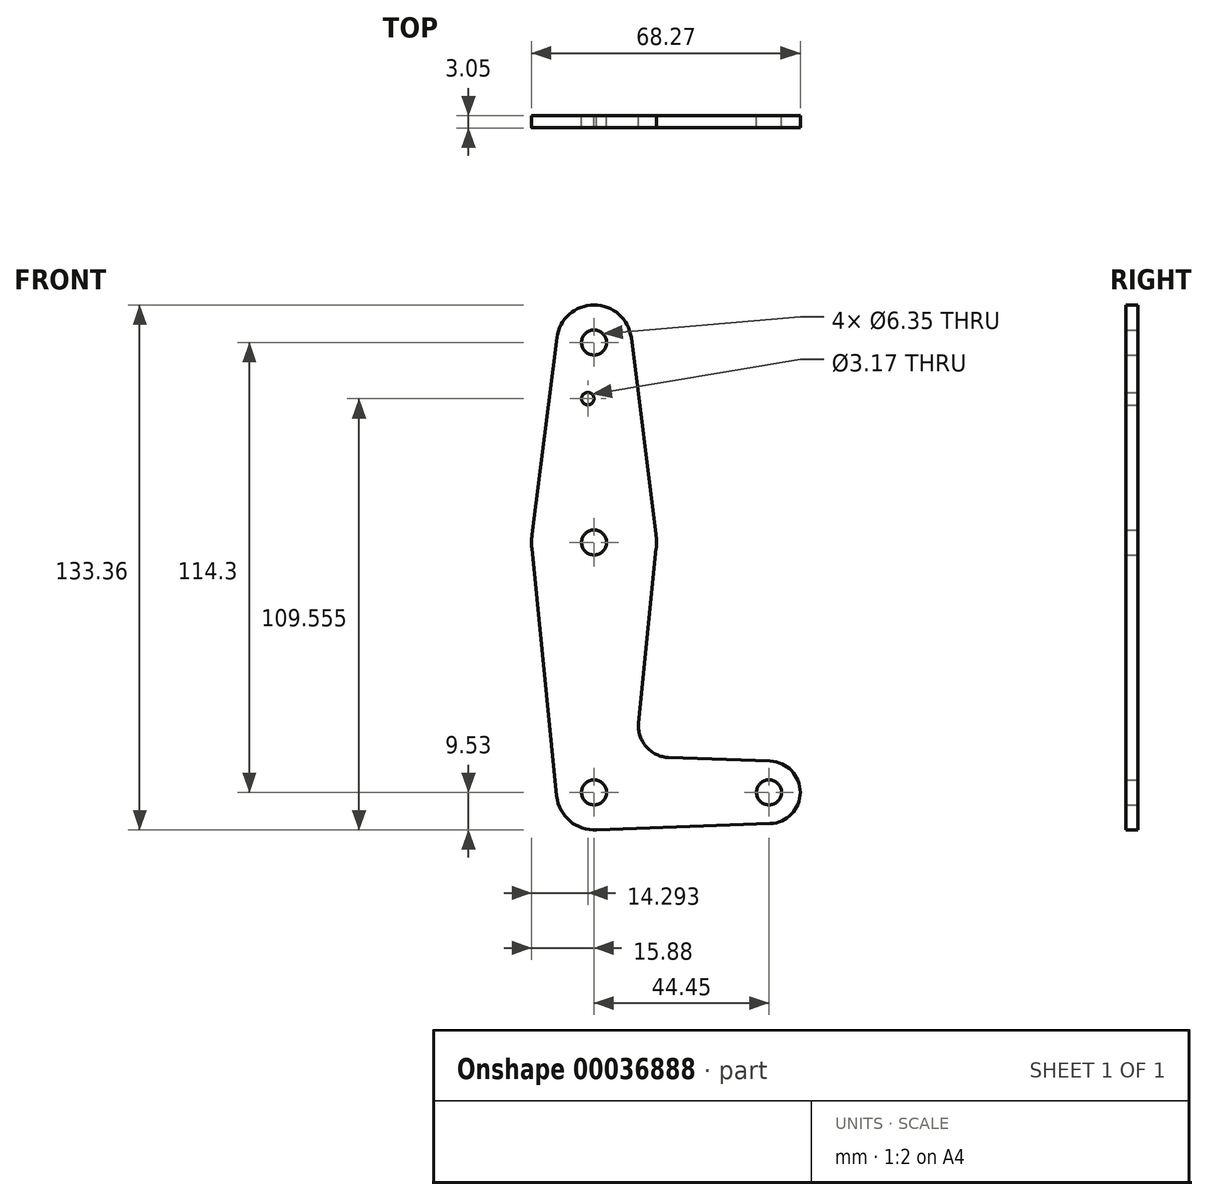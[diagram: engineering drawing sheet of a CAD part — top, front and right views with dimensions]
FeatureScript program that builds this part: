
annotation { "Feature Type Name" : "Feature", "Feature Type Description" : "" }
export const myFeature = defineFeature(function(context is Context, id is Id, definition is map)
    precondition{}
    {
        {
            var Q0;
            Q0=qCreatedBy(makeId("Front.planeOp"),FACE);
            var sketch = newSketch(context, id + "F0", { "sketchPlane" : qUnion([Q0])});
            skLineSegment(sketch, "E0", {"start": v(0, 0) * mm, "end": v(44.45, 0) * mm});
            skCircle(sketch, "E1", {"center": v(0, 114.3) * mm, "radius": 9.53 * mm});
            skCircle(sketch, "E2", {"center": v(0, 0) * mm, "radius": 9.53 * mm});
            skCircle(sketch, "E3", {"center": v(44.45, 0) * mm, "radius": 7.94 * mm});
            skCircle(sketch, "E4", {"center": v(0, 63.5) * mm, "radius": 15.88 * mm});
            skLineSegment(sketch, "E5", {"start": v(-9.45, 115.5) * mm, "end": v(-15.75, 65.48) * mm});
            skLineSegment(sketch, "E6", {"start": v(0, -9.53) * mm, "end": v(44.73, -7.93) * mm});
            skLineSegment(sketch, "E7", {"start": v(9.45, 115.5) * mm, "end": v(15.75, 65.48) * mm});
            skLineSegment(sketch, "E8", {"start": v(-15.8, 61.91) * mm, "end": v(-9.48, -0.95) * mm});
            skCircle(sketch, "E9", {"center": v(0, 114.3) * mm, "radius": 3.18 * mm});
            skLineSegment(sketch, "E10", {"start": v(18.97, 8.85) * mm, "end": v(44.73, 7.93) * mm});
            skLineSegment(sketch, "E11", {"start": v(0, 114.3) * mm, "end": v(0, 0) * mm, "construction": true});
            skCircle(sketch, "E12", {"center": v(0, 63.5) * mm, "radius": 3.18 * mm});
            skCircle(sketch, "E13", {"center": v(0, 0) * mm, "radius": 3.18 * mm});
            skCircle(sketch, "E14", {"center": v(44.45, 0) * mm, "radius": 3.18 * mm});
            skLineSegment(sketch, "E15", {"start": v(15.8, 61.91) * mm, "end": v(11.34, 17.6) * mm});
            skArc(sketch, "E16.filletArc", {"start": v(11.34, 17.6) * mm, "mid": v(13.26, 11.57) * mm, "end": v(18.97, 8.85) * mm});
            skCircle(sketch, "E17", {"center": v(-1.59, 100.03) * mm, "radius": 1.59 * mm});
            skSolve(sketch);
        }
        {
            var Q0;
            Q0 = qSketchRegion(id + "F0", true);
            extrude(context, id + "F1", {"entities" : qUnion([Q0]), "depth" : 3.05 * mm});
        }
    });
